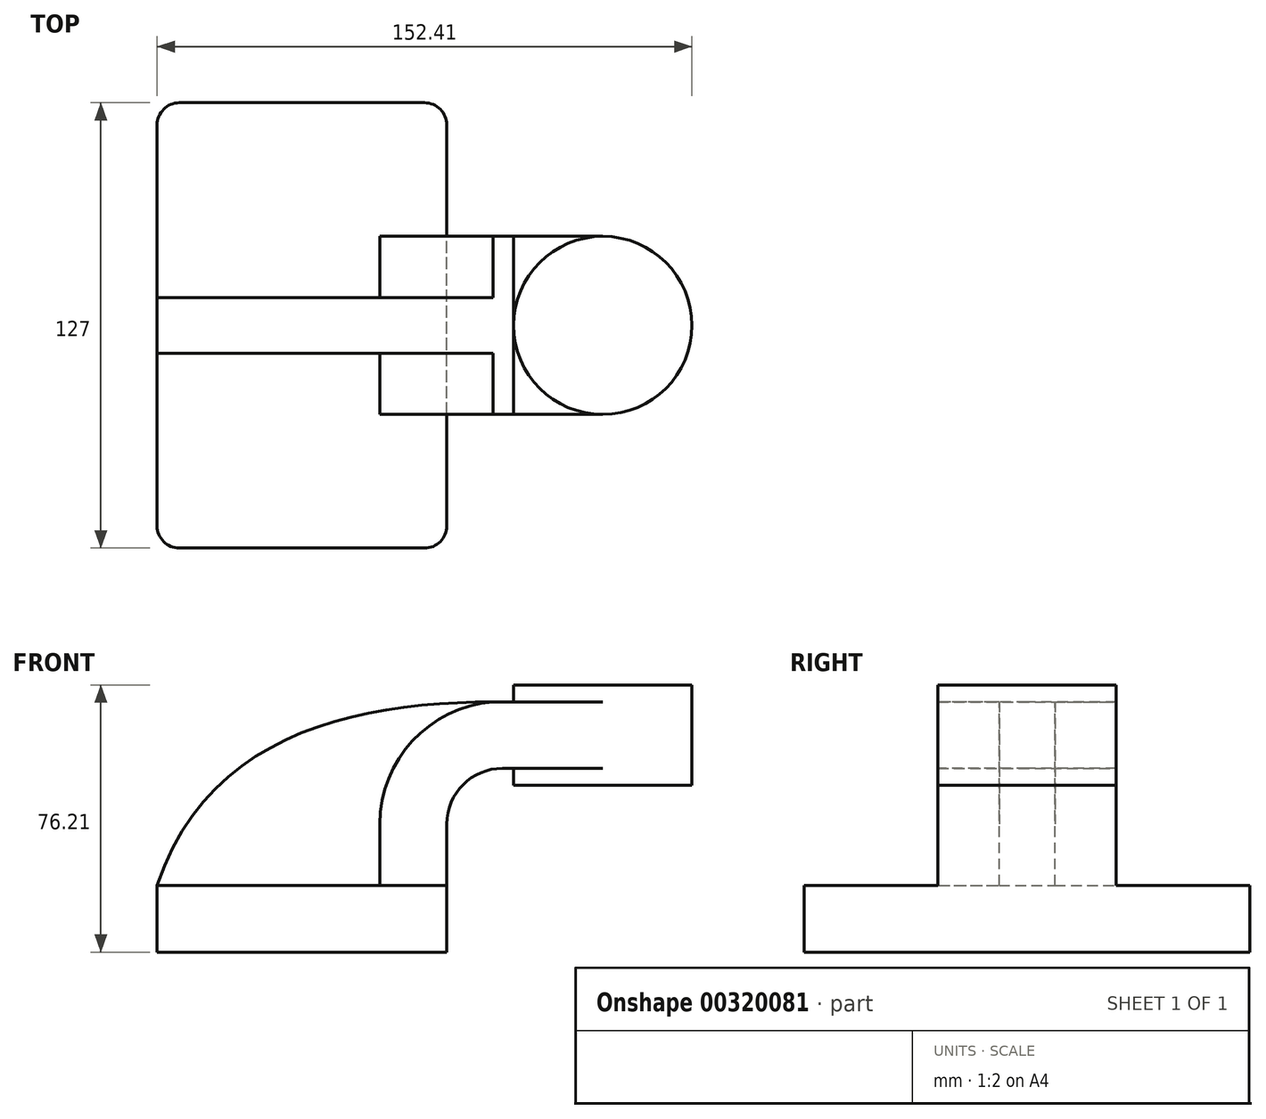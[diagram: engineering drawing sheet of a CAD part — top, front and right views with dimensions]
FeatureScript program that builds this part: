
annotation { "Feature Type Name" : "Feature", "Feature Type Description" : "" }
export const myFeature = defineFeature(function(context is Context, id is Id, definition is map)
    precondition{}
    {
        {
            var Q0;
            Q0=qCreatedBy(makeId("Front.planeOp"),FACE);
            var sketch = newSketch(context, id + "F0", { "sketchPlane" : qUnion([Q0])});
            skLineSegment(sketch, "E0.bottom", {"start": v(41.28, -9.52) * mm, "end": v(-41.28, -9.53) * mm});
            skLineSegment(sketch, "E0.top", {"start": v(41.28, 9.53) * mm, "end": v(-41.28, 9.52) * mm});
            skLineSegment(sketch, "E0.left", {"start": v(41.28, -9.52) * mm, "end": v(41.28, 9.53) * mm});
            skLineSegment(sketch, "E0.right", {"start": v(-41.28, -9.53) * mm, "end": v(-41.28, 9.52) * mm});
            skPoint(sketch, "E0.middle", {"position": v(0, 0) * mm});
            skLineSegment(sketch, "E1.bottom", {"start": v(111.12, 38.1) * mm, "end": v(60.33, 38.1) * mm});
            skLineSegment(sketch, "E1.top", {"start": v(111.12, 66.68) * mm, "end": v(60.33, 66.68) * mm});
            skLineSegment(sketch, "E1.left", {"start": v(111.12, 38.1) * mm, "end": v(111.12, 66.68) * mm});
            skLineSegment(sketch, "E1.right", {"start": v(60.33, 38.1) * mm, "end": v(60.33, 66.68) * mm});
            skPoint(sketch, "E1.middle", {"position": v(85.72, 52.39) * mm});
            skLineSegment(sketch, "E2", {"start": v(41.28, 9.53) * mm, "end": v(41.28, 27) * mm});
            skArc(sketch, "E3", {"start": v(41.28, 27) * mm, "mid": v(45.92, 38.23) * mm, "end": v(57.15, 42.88) * mm});
            skLineSegment(sketch, "E4", {"start": v(57.15, 42.88) * mm, "end": v(85.72, 42.88) * mm});
            skArc(sketch, "E5.0", {"start": v(22.23, 27) * mm, "mid": v(33.6, 52.8) * mm, "end": v(60.33, 61.78) * mm});
            skLineSegment(sketch, "E5.1", {"start": v(22.23, 9.53) * mm, "end": v(22.23, 27) * mm});
            skLineSegment(sketch, "E6", {"start": v(85.72, 38.1) * mm, "end": v(85.72, 66.68) * mm});
            skFitSpline(sketch, "E7", {"points": [v(-41.28, 9.52) * mm, v(60.32, 61.78) * mm], "startDerivative": vector(46.43, 138) * mm, "endDerivative": vector(120.32, -1.95) * mm});
            skLineSegment(sketch, "E8", {"start": v(60.33, 61.78) * mm, "end": v(85.72, 61.78) * mm});
            skSolve(sketch);
        }
        {
            var Q0;
            Q0=makeQuery(id+"F0.imprint","IMPRINT",FACE,{"disambiguationData":[TD([[makeQuery(id+"F0.imprint","IMPRINT",EDGE,{"derivedFrom":sQuery(id+"F0.wireOp",EDGE,"E0.bottom")}),-1.0]])]});
            extrude(context, id + "F1", {"entities" : qUnion([Q0]), "endBound" : BoundingType.SYMMETRIC, "depth" : 127 * mm});
        }
        {
            var Q0;
            {var subQ1=sQuery(id+"F0.wireOp",EDGE,"E2");Q0=makeQuery(id+"F0.imprint","IMPRINT",FACE,{"disambiguationData":[TD([[makeQuery(id+"F0.imprint","IMPRINT",EDGE,{"derivedFrom":subQ1}),1.0]])]});}
            var Q1;
            {var subQ0=sQuery(id+"F0.wireOp",EDGE,"E8");Q1=makeQuery(id+"F0.imprint","IMPRINT",FACE,{"disambiguationData":[TD([[makeQuery(id+"F0.imprint","IMPRINT",EDGE,{"derivedFrom":subQ0}),-1.0]])]});}
            extrude(context, id + "F2", {"entities" : qUnion([Q0, Q1]), "operationType" : NewBodyOperationType.ADD, "endBound" : BoundingType.SYMMETRIC, "depth" : 50.8 * mm});
        }
        {
            var Q0;
            {var subQ3=sQuery(id+"F0.wireOp",EDGE,"E5.1");Q0=makeQuery(id+"F0.imprint","IMPRINT",FACE,{"disambiguationData":[TD([[makeQuery(id+"F0.imprint","IMPRINT",EDGE,{"derivedFrom":subQ3}),1.0]])]});}
            extrude(context, id + "F3", {"entities" : qUnion([Q0]), "operationType" : NewBodyOperationType.ADD, "endBound" : BoundingType.SYMMETRIC, "depth" : 15.88 * mm});
        }
        {
            var Q0;
            {var subQ0=sQuery(id+"F0.wireOp",EDGE,"E1.left");Q0=makeQuery(id+"F0.imprint","IMPRINT",FACE,{"disambiguationData":[TD([[makeQuery(id+"F0.imprint","IMPRINT",EDGE,{"derivedFrom":subQ0}),1.0]])]});}
            var Q1;
            Q1=sQuery(id+"F0.wireOp",EDGE,"E6");
            revolve(context, id + "F4", {"operationType" : NewBodyOperationType.ADD, "entities" : qUnion([Q0]), "axis" : qUnion([Q1]), "revolveType" : RevolveType.FULL});
        }
        {
            var Q0;
            Q0=makeQuery(id+"F1.opExtrude","CAP_EDGE",EDGE,{"disambiguationData":[OSD([sQuery(id+"F0.wireOp",EDGE,"E0.left")])],"isStart":false});
            var Q1;
            Q1=makeQuery(id+"F1.opExtrude","CAP_EDGE",EDGE,{"disambiguationData":[OSD([sQuery(id+"F0.wireOp",EDGE,"E0.right")])],"isStart":false});
            var Q2;
            Q2=makeQuery(id+"F1.opExtrude","CAP_EDGE",EDGE,{"disambiguationData":[OSD([sQuery(id+"F0.wireOp",EDGE,"E0.right")])],"isStart":true});
            var Q3;
            Q3=makeQuery(id+"F1.opExtrude","CAP_EDGE",EDGE,{"disambiguationData":[OSD([sQuery(id+"F0.wireOp",EDGE,"E0.left")])],"isStart":true});
            fillet(context, id + "F5", {"entities" : qUnion([Q0, Q1, Q2, Q3]), "radius" : 6.35 * mm, "tangentPropagation" : true, "allowEdgeOverflow" : false});
        }
    });
